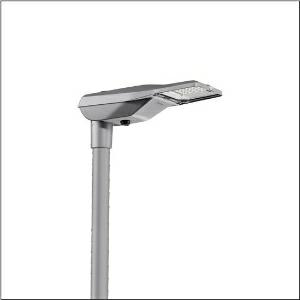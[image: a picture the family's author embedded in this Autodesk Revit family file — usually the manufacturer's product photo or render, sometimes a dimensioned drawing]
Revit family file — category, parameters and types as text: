
# Revit family: streetlight_sl_21_iq_micro___p0_8a_5xe1u31u08db_b9e4
name_source: partatom
category: Lighting Fixtures
units: mm (PartAtom-declared; Revit-internal decimal feet)

## family parameters
Cut with Voids When Loaded = No
Host = Face
Light Source = No
Part Type = Normal
Room Calculation Point = No
Round Connector Dimension = Use Diameter
Shared = No

## types (1)
- --- (1 x LED, 5130 lm, 39.1 W, 3000K)
    Apparent Load = 39 VA
    CIE Flux Codes = 33 69 96 100 100
    Color Rendering = 70
    Color Temperature = 3000K
    Default Elevation = 1800 mm
    Description = Streetlight SL 21 iQ micro, mast luminaire, primary light control with lens, of PMMA, primary optical cover: cover, of toughened safety glass, transparent, light distribution: P0.8a, light emission: direct distribution, primary light characteristic: asymmetric, installation type: post-top, side-entry, LED, High Power LED, rated luminous flux: 5.130lm, luminous efficacy: 131lm/W, light colour: 730, colour temperature: 3000K, control gear: iQ-Street Remote, D4i with power reduction, control: pre-setting: logarithmic dimming characteristic, Street-Remote, Auto-Match, Temp-Guard, Lumen-Switch, Night-Set, Smart-Wire, Light-Fading, Desk-Remote (wireless, voltage-free reading and setting of iQ features in the workshop via application-optimized NFC function/RFID function), optimised constant luminous flux control (CLO 2.0), mains connection: 220..240V, AC, 50/60Hz, start of lifetime: 39W, end of service life: 41W, reduction: 17W, luminaire housing, of diecast aluminium, powder-coated, Siteco® metallic grey (DB 702S), corrosivity category C5 mid according to DIN EN ISO 12944, please order mast flange separately, inclination adjustable: 0°, 5°, 10°, 15°, sealing non-destructively replaceable, multi-level sealing system, length: 528mm, width: 235mm, height: 110mm, mast flange for spigot size: 42mm (side-entry): 5XC10008XM4, 60/48mm (side-entry/post-top): 5XC10108XM2, 76/60mm (side-entry/post-top): 5XC10108XM1, mounting height: 4..8m, Smart Interface below, protection rating (complete): IP66, insulation class (complete): insulation class II (safety insulation), certification: CE, ENEC, ENEC+, VDE, impact resistance: IK10, permissible operating ambient temperature for outdoor applications: -40..+50°C, standard-compliant lighting for roads and squares, packaging unit: 1 piece

Light Distribution: P0.8a
    Height = 110 mm
    Lamp = 1 x LED
    Lamp Light Flux = 5130 lm
    Lamp Power = 39.1 W
    Lamp count = 1
    Length = 528 mm
    Luminous efficacy = 131 lm/W
    Manufacturer = Siteco
    ModVariant = No
    Model = 5XE1U31U08DB
    Number of Poles = 1
    OnlyDefault = Yes
    Power Factor = 1
    Product Name = Streetlight SL 21 iQ micro | P0.8a
    Product group = mast luminaire | pylon top
    ProductGroupID = 6100
    Protection Class = Protection class II
    Protection Degree = IP 66
    RLX_Detail_Level = 1
    RLX_Emergency_Light_Flux = 0 lm
    RLX_Emergency_Type = 0
    RLX_Emergency_Type_DB = No
    RlxData = <blob elided: 98705 chars, md5=8e673f1f>
    Socket = socket
    Standby Power = 0 W
    System Light Flux = 5130 lm
    System Power = 39 W
    Type Comments = factory setting: luminous flux: 100 % | dim-lin: 254 | 765 mA
    Type Image = l_1277290.jpg
    URL = http://relux.com
    VarID = @adj_074332
    Voltage = 0 V
    Weight = 0.00 kg
    Width = 235 mm

## geometry (parser evidence)
native form markers: Blend x4, Sweep x10
no freeform markers — native parametric forms only
